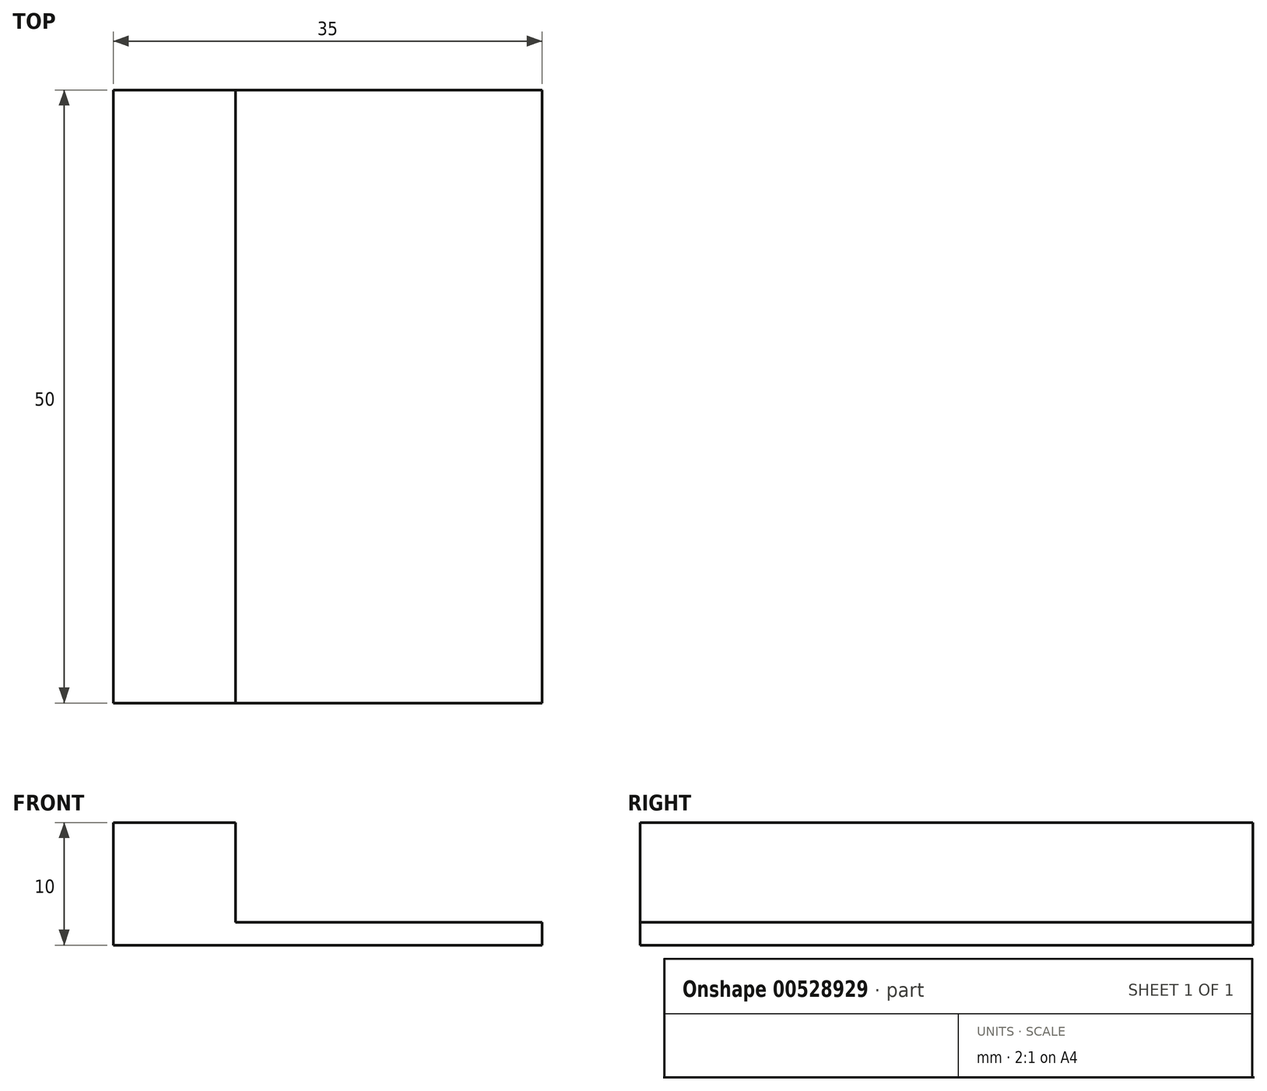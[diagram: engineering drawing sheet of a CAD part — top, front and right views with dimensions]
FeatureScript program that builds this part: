
annotation { "Feature Type Name" : "Feature", "Feature Type Description" : "" }
export const myFeature = defineFeature(function(context is Context, id is Id, definition is map)
    precondition{}
    {
        {
            var Q0;
            Q0=qCreatedBy(makeId("Top.planeOp"),FACE);
            var sketch = newSketch(context, id + "F0", { "sketchPlane" : qUnion([Q0])});
            skLineSegment(sketch, "E0.bottom", {"start": v(-66.46, 7.43) * mm, "end": v(-76.46, 7.43) * mm});
            skLineSegment(sketch, "E0.top", {"start": v(-66.46, 57.43) * mm, "end": v(-76.46, 57.43) * mm});
            skLineSegment(sketch, "E0.left", {"start": v(-66.46, 7.43) * mm, "end": v(-66.46, 57.43) * mm});
            skLineSegment(sketch, "E0.right", {"start": v(-76.46, 7.43) * mm, "end": v(-76.46, 57.43) * mm});
            skPoint(sketch, "E0.middle", {"position": v(-71.46, 32.43) * mm});
            skSolve(sketch);
        }
        {
            var Q0;
            Q0 = qSketchRegion(id + "F0", true);
            extrude(context, id + "F1", {"entities" : qUnion([Q0]), "depth" : 10 * mm, "offsetDistance" : 25 * mm});
        }
        {
            var Q0;
            Q0=makeQuery(id+"F1.opExtrude","SWEPT_FACE",FACE,{"disambiguationData":[OSD([sQuery(id+"F0.wireOp",EDGE,"E0.left")])]});
            var sketch = newSketch(context, id + "F2", { "sketchPlane" : qUnion([Q0])});
            skLineSegment(sketch, "E1.bottom", {"start": v(7.43, 0) * mm, "end": v(57.43, 0) * mm});
            skLineSegment(sketch, "E1.top", {"start": v(7.43, 1.87) * mm, "end": v(57.43, 1.87) * mm});
            skLineSegment(sketch, "E1.left", {"start": v(7.43, 0) * mm, "end": v(7.43, 1.87) * mm});
            skLineSegment(sketch, "E1.right", {"start": v(57.43, 0) * mm, "end": v(57.43, 1.87) * mm});
            skSolve(sketch);
        }
        {
            var Q0;
            Q0 = qSketchRegion(id + "F2", true);
            extrude(context, id + "F3", {"entities" : qUnion([Q0]), "operationType" : NewBodyOperationType.ADD, "depth" : 25 * mm, "offsetDistance" : 25 * mm});
        }
    });
